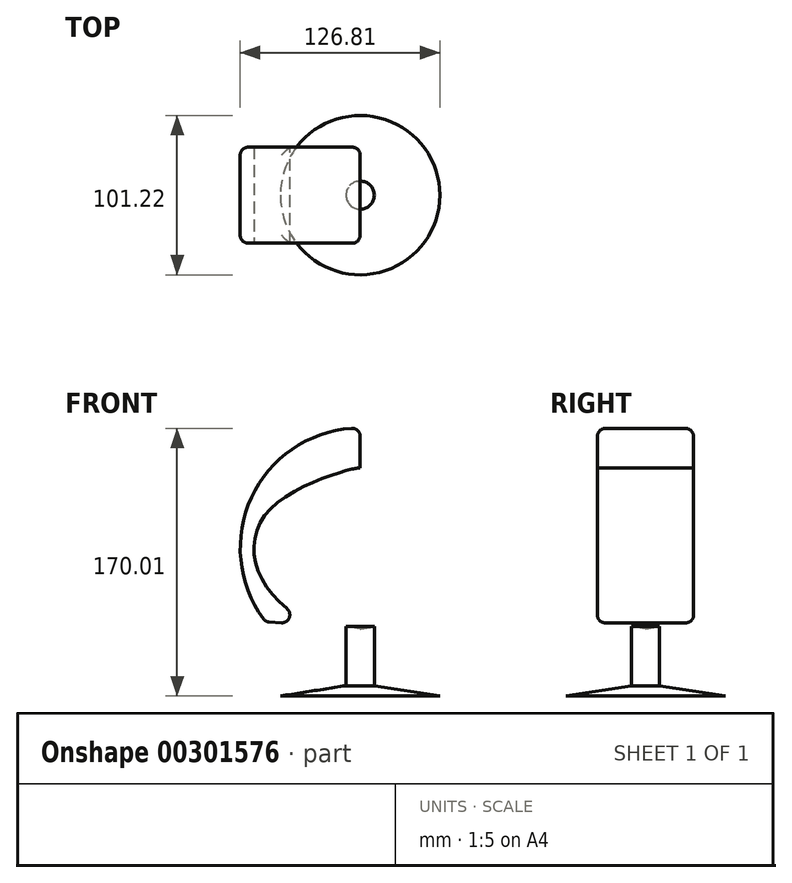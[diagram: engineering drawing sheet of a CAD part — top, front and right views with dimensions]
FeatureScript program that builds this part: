
annotation { "Feature Type Name" : "Feature", "Feature Type Description" : "" }
export const myFeature = defineFeature(function(context is Context, id is Id, definition is map)
    precondition{}
    {
        {
            var Q0;
            Q0=qCreatedBy(makeId("Front.planeOp"),FACE);
            var sketch = newSketch(context, id + "F0", { "sketchPlane" : qUnion([Q0])});
            skArc(sketch, "E0", {"start": v(0, 76.2) * mm, "mid": v(-68.47, 33.44) * mm, "end": v(-60.1, -46.85) * mm});
            skLineSegment(sketch, "E1", {"start": v(0, 76.2) * mm, "end": v(0, 50.82) * mm});
            skFitSpline(sketch, "E2", {"points": [v(0, 50.82) * mm, v(-28.65, 35.5) * mm, v(-37.4, 5.84) * mm, v(-21.4, -22.78) * mm, v(44.23, -18.32) * mm, v(54, -53.77) * mm, v(-45.52, -39.3) * mm, v(-57.8, 23.94) * mm, v(0, 50.82) * mm]});
            skLineSegment(sketch, "E3", {"start": v(54, -53.77) * mm, "end": v(-60.1, -46.85) * mm});
            skLineSegment(sketch, "E4", {"start": v(0, 73.33) * mm, "end": v(4.13, 73.33) * mm});
            skLineSegment(sketch, "E5", {"start": v(4.13, 73.33) * mm, "end": v(4.13, 52.67) * mm});
            skLineSegment(sketch, "E6", {"start": v(4.13, 52.67) * mm, "end": v(0, 50.82) * mm});
            skLineSegment(sketch, "E7", {"start": v(50.05, -22.1) * mm, "end": v(50.05, -14.81) * mm});
            skLineSegment(sketch, "E8", {"start": v(50.05, -14.81) * mm, "end": v(9.64, -14.81) * mm});
            skLineSegment(sketch, "E9", {"start": v(9.64, -14.81) * mm, "end": v(9.64, -18.32) * mm});
            skLineSegment(sketch, "E10", {"start": v(9.64, -18.32) * mm, "end": v(13.5, -18.68) * mm});
            skSolve(sketch);
        }
        {
            var Q0;
            Q0=qCreatedBy(makeId("Front.planeOp"),FACE);
            var sketch = newSketch(context, id + "F1", { "sketchPlane" : qUnion([Q0])});
            skLineSegment(sketch, "E11", {"start": v(0, -51.3) * mm, "end": v(0, -86.41) * mm, "construction": true});
            skLineSegment(sketch, "E12", {"start": v(-8.95, -49.92) * mm, "end": v(-8.95, -87.45) * mm});
            skLineSegment(sketch, "E13", {"start": v(-8.95, -87.45) * mm, "end": v(-50.6, -93.99) * mm});
            skLineSegment(sketch, "E14", {"start": v(-50.6, -93.99) * mm, "end": v(0, -93.99) * mm});
            skLineSegment(sketch, "E15", {"start": v(0, -93.99) * mm, "end": v(0, -51.3) * mm});
            skLineSegment(sketch, "E16", {"start": v(0, -51.3) * mm, "end": v(-8.95, -49.92) * mm});
            skSolve(sketch);
        }
        {
            var Q0;
            Q0=makeQuery(id+"F1.imprint","IMPRINT",FACE,{"disambiguationData":[TD([[makeQuery(id+"F1.imprint","IMPRINT",EDGE,{"derivedFrom":sQuery(id+"F1.wireOp",EDGE,"E12")}),1.0]])]});
            var Q1;
            Q1=sQuery(id+"F1.wireOp",EDGE,"E15");
            revolve(context, id + "F2", {"entities" : qUnion([Q0]), "axis" : qUnion([Q1]), "revolveType" : RevolveType.FULL});
        }
        {
            var Q0;
            {var subQ5=sQuery(id+"F0.wireOp",EDGE,"E0");Q0=makeQuery(id+"F0.imprint","IMPRINT",FACE,{"disambiguationData":[TD([[makeQuery(id+"F0.imprint","IMPRINT",EDGE,{"derivedFrom":subQ5}),1.0]])]});}
            extrude(context, id + "F3", {"entities" : qUnion([Q0]), "operationType" : NewBodyOperationType.ADD, "endBound" : BoundingType.SYMMETRIC, "depth" : 60.96 * mm});
        }
        {
            var Q0;
            Q0=makeQuery(id+"F3.opExtrude","CAP_EDGE",EDGE,{"disambiguationData":[OSD([sQuery(id+"F0.wireOp",EDGE,"E1")])],"isStart":false});
            var Q1;
            Q1=makeQuery(id+"F3.opExtrude","SWEPT_FACE",FACE,{"disambiguationData":[OSD([sQuery(id+"F0.wireOp",EDGE,"E0")])]});
            var Q2;
            Q2=makeQuery(id+"F3.opExtrude","CAP_EDGE",EDGE,{"disambiguationData":[OSD([sQuery(id+"F0.wireOp",EDGE,"E1")])],"isStart":true});
            var Q3;
            Q3=makeQuery(id+"F3.opExtrude","CAP_EDGE",EDGE,{"disambiguationData":[OSD([sQuery(id+"F0.wireOp",EDGE,"E3")])],"isStart":true});
            var Q4;
            Q4=makeQuery(id+"F3.opExtrude","CAP_EDGE",EDGE,{"disambiguationData":[OSD([sQuery(id+"F0.wireOp",EDGE,"E3")])],"isStart":false});
            var Q5;
            Q5=makeQuery(id+"F3.opExtrude","SWEPT_EDGE",EDGE,{"disambiguationData":[OSD([sQuery(id+"F0.wireOp",EDGE,"E2"),sQuery(id+"F0.wireOp",EDGE,"E3")])]});
            fillet(context, id + "F4", {"entities" : qUnion([Q0, Q1, Q2, Q3, Q4, Q5]), "radius" : 5.08 * mm, "tangentPropagation" : true, "allowEdgeOverflow" : false});
        }
    });
